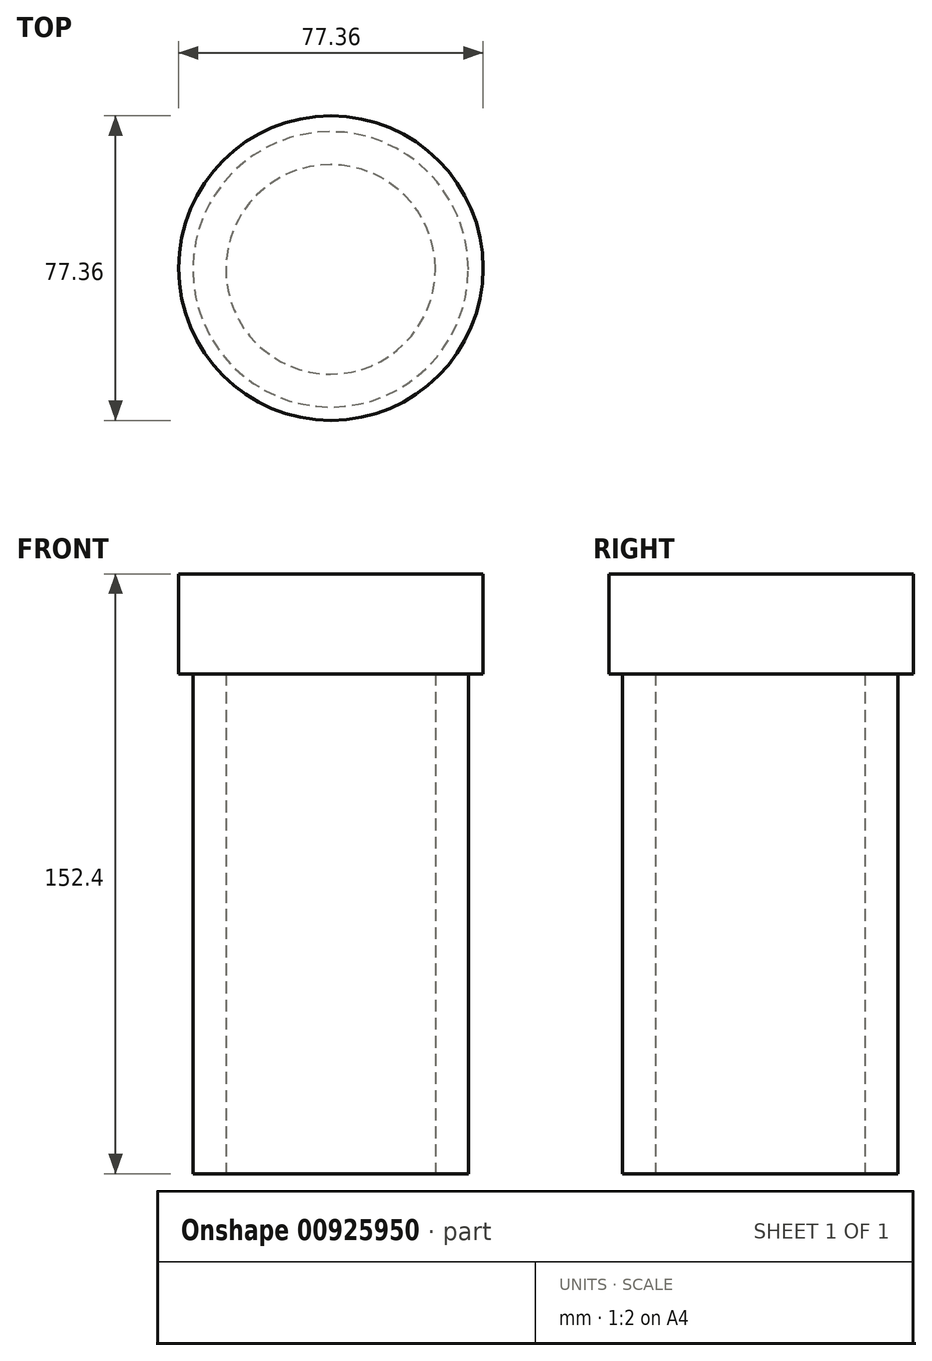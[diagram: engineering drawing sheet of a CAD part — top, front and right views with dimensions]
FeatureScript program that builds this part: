
annotation { "Feature Type Name" : "Feature", "Feature Type Description" : "" }
export const myFeature = defineFeature(function(context is Context, id is Id, definition is map)
    precondition{}
    {
        {
            var Q0;
            Q0=qCreatedBy(makeId("Top.planeOp"),FACE);
            var sketch = newSketch(context, id + "F0", { "sketchPlane" : qUnion([Q0])});
            skCircle(sketch, "E0", {"center": v(-52.78, 21.8) * mm, "radius": 34.98 * mm});
            skCircle(sketch, "E1", {"center": v(-52.78, 21.8) * mm, "radius": 26.62 * mm});
            skSolve(sketch);
        }
        {
            var Q0;
            Q0 = qSketchRegion(id + "F0", true);
            extrude(context, id + "F1", {"entities" : qUnion([Q0]), "depth" : 127 * mm, "offsetDistance" : 25.4 * mm});
        }
        {
            var Q0;
            Q0=makeQuery(id+"F1.opExtrude","CAP_FACE",FACE,{"disambiguationData":[OSD([sQuery(id+"F0.wireOp",EDGE,"E0"),sQuery(id+"F0.wireOp",EDGE,"E1")])],"isStart":false});
            var sketch = newSketch(context, id + "F2", { "sketchPlane" : qUnion([Q0])});
            skCircle(sketch, "E2", {"center": v(-52.78, 21.8) * mm, "radius": 35.45 * mm});
            skSolve(sketch);
        }
        {
            var Q0;
            Q0=makeQuery(id+"F2.imprint","IMPRINT",FACE,{"disambiguationData":[TD([[makeQuery(id+"F2.imprint","IMPRINT",EDGE,{"derivedFrom":makeQuery(id+"F1.opExtrude","CAP_EDGE",EDGE,{"disambiguationData":[OSD([sQuery(id+"F0.wireOp",EDGE,"E0")])],"isStart":false})}),1.0]])]});
            var sketch = newSketch(context, id + "F3", { "sketchPlane" : qUnion([Q0])});
            skCircle(sketch, "E3", {"center": v(-52.71, 22.12) * mm, "radius": 38.68 * mm});
            skSolve(sketch);
        }
        {
            var Q0;
            Q0 = qSketchRegion(id + "F3", true);
            extrude(context, id + "F4", {"entities" : qUnion([Q0]), "operationType" : NewBodyOperationType.ADD, "depth" : 25.4 * mm, "offsetDistance" : 25.4 * mm});
        }
    });
